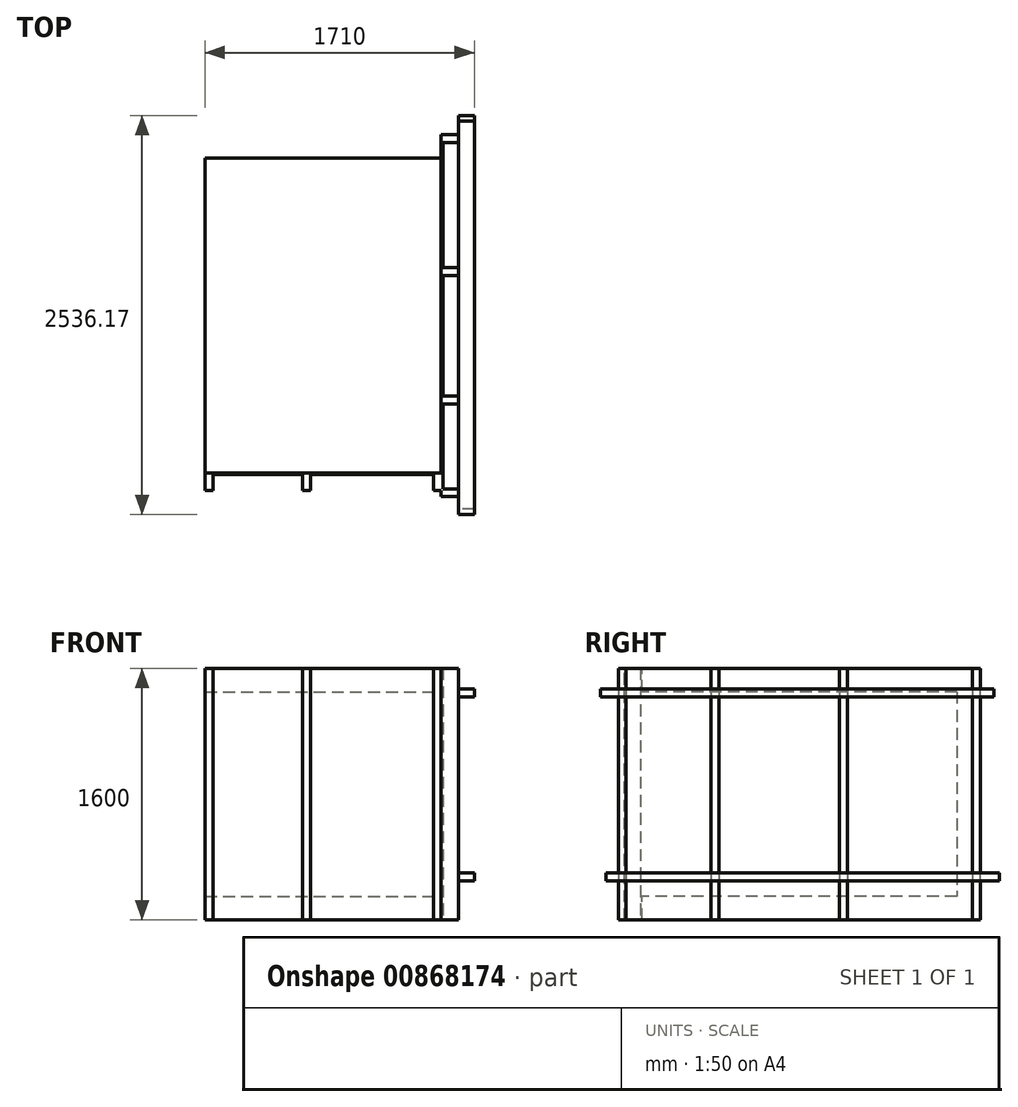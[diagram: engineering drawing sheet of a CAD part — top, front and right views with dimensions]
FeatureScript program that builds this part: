
annotation { "Feature Type Name" : "Feature", "Feature Type Description" : "" }
export const myFeature = defineFeature(function(context is Context, id is Id, definition is map)
    precondition{}
    {
        {
            var Q0;
            Q0=qCreatedBy(makeId("Top.planeOp"),FACE);
            var sketch = newSketch(context, id + "F0", { "sketchPlane" : qUnion([Q0])});
            skLineSegment(sketch, "E0.bottom", {"start": v(-1448.2, 1942.9) * mm, "end": v(51.8, 1942.9) * mm});
            skLineSegment(sketch, "E0.top", {"start": v(-1448.2, -57.1) * mm, "end": v(51.8, -57.1) * mm});
            skLineSegment(sketch, "E0.left", {"start": v(-1448.2, 1942.9) * mm, "end": v(-1448.2, -57.1) * mm});
            skLineSegment(sketch, "E0.right", {"start": v(51.8, 1942.9) * mm, "end": v(51.8, -57.1) * mm});
            skSolve(sketch);
        }
        {
            var Q0;
            Q0=makeQuery(id+"F0.imprint","IMPRINT",FACE,{"disambiguationData":[TD([[makeQuery(id+"F0.imprint","IMPRINT",EDGE,{"derivedFrom":sQuery(id+"F0.wireOp",EDGE,"E0.bottom")}),-1.0]])]});
            extrude(context, id + "F1", {"entities" : qUnion([Q0]), "depth" : 1300 * mm, "offsetDistance" : 25 * mm});
        }
        {
            var Q0;
            Q0=makeQuery(id+"F1.opExtrude","SWEPT_FACE",FACE,{"disambiguationData":[OSD([sQuery(id+"F0.wireOp",EDGE,"E0.right")])]});
            var sketch = newSketch(context, id + "F2", { "sketchPlane" : qUnion([Q0])});
            skLineSegment(sketch, "E1.bottom", {"start": v(-57.1, 1300) * mm, "end": v(1942.9, 1300) * mm});
            skLineSegment(sketch, "E1.top", {"start": v(-57.1, 0) * mm, "end": v(1942.9, 0) * mm});
            skLineSegment(sketch, "E1.left", {"start": v(-57.1, 1300) * mm, "end": v(-57.1, 0) * mm});
            skLineSegment(sketch, "E1.right", {"start": v(1942.9, 1300) * mm, "end": v(1942.9, 0) * mm});
            skLineSegment(sketch, "E2.0", {"start": v(-207.1, -150) * mm, "end": v(2092.9, -150) * mm});
            skLineSegment(sketch, "E2.1", {"start": v(-207.1, 1450) * mm, "end": v(-207.1, -150) * mm});
            skLineSegment(sketch, "E2.2", {"start": v(2092.9, 1450) * mm, "end": v(-207.1, 1450) * mm});
            skLineSegment(sketch, "E2.3", {"start": v(2092.9, -150) * mm, "end": v(2092.9, 1450) * mm});
            skSolve(sketch);
        }
        {
            var Q0;
            Q0=makeQuery(id+"F2.imprint","IMPRINT",FACE,{"disambiguationData":[TD([[makeQuery(id+"F2.imprint","IMPRINT",EDGE,{"derivedFrom":sQuery(id+"F2.wireOp",EDGE,"E1.bottom")}),-1.0]])]});
            var Q1;
            Q1=makeQuery(id+"F2.imprint","IMPRINT",FACE,{"disambiguationData":[TD([[makeQuery(id+"F2.imprint","IMPRINT",EDGE,{"derivedFrom":sQuery(id+"F2.wireOp",EDGE,"E1.bottom")}),1.0]])]});
            extrude(context, id + "F3", {"entities" : qUnion([Q0, Q1]), "operationType" : NewBodyOperationType.ADD, "depth" : 10 * mm, "offsetDistance" : 25 * mm});
        }
        {
            var Q0;
            Q0=makeQuery(id+"F3.opExtrude","CAP_FACE",FACE,{"disambiguationData":[OSD([sQuery(id+"F2.wireOp",EDGE,"E2.0"),sQuery(id+"F2.wireOp",EDGE,"E2.1"),sQuery(id+"F2.wireOp",EDGE,"E2.2"),sQuery(id+"F2.wireOp",EDGE,"E2.3")])],"isStart":false});
            var sketch = newSketch(context, id + "F4", { "sketchPlane" : qUnion([Q0])});
            skLineSegment(sketch, "E3.bottom", {"start": v(-207.1, 1450) * mm, "end": v(-157.1, 1450) * mm});
            skLineSegment(sketch, "E3.top", {"start": v(-207.1, -150) * mm, "end": v(-157.1, -150) * mm});
            skLineSegment(sketch, "E3.left", {"start": v(-207.1, 1450) * mm, "end": v(-207.1, -150) * mm});
            skLineSegment(sketch, "E3.right", {"start": v(-157.1, 1450) * mm, "end": v(-157.1, -150) * mm});
            skLineSegment(sketch, "E4.bottom", {"start": v(2042.9, 1450) * mm, "end": v(2092.9, 1450) * mm});
            skLineSegment(sketch, "E4.top", {"start": v(2042.9, -150) * mm, "end": v(2092.9, -150) * mm});
            skLineSegment(sketch, "E4.left", {"start": v(2042.9, 1450) * mm, "end": v(2042.9, -150) * mm});
            skLineSegment(sketch, "E4.right", {"start": v(2092.9, 1450) * mm, "end": v(2092.9, -150) * mm});
            skLineSegment(sketch, "E5.bottom", {"start": v(381.46, 1450) * mm, "end": v(431.46, 1450) * mm});
            skLineSegment(sketch, "E5.top", {"start": v(381.46, -150) * mm, "end": v(431.46, -150) * mm});
            skLineSegment(sketch, "E5.left", {"start": v(381.46, 1450) * mm, "end": v(381.46, -150) * mm});
            skLineSegment(sketch, "E5.right", {"start": v(431.46, 1450) * mm, "end": v(431.46, -150) * mm});
            skLineSegment(sketch, "E6.bottom", {"start": v(1197.73, 1450) * mm, "end": v(1247.73, 1450) * mm});
            skLineSegment(sketch, "E6.top", {"start": v(1197.73, -150) * mm, "end": v(1247.73, -150) * mm});
            skLineSegment(sketch, "E6.left", {"start": v(1197.73, 1450) * mm, "end": v(1197.73, -150) * mm});
            skLineSegment(sketch, "E6.right", {"start": v(1247.73, 1450) * mm, "end": v(1247.73, -150) * mm});
            skSolve(sketch);
        }
        {
            var Q0;
            Q0=makeQuery(id+"F4.imprint","IMPRINT",FACE,{"disambiguationData":[TD([[makeQuery(id+"F4.imprint","IMPRINT",EDGE,{"derivedFrom":sQuery(id+"F4.wireOp",EDGE,"E3.bottom")}),1.0]])]});
            var Q1;
            Q1=makeQuery(id+"F4.imprint","IMPRINT",FACE,{"disambiguationData":[TD([[makeQuery(id+"F4.imprint","IMPRINT",EDGE,{"derivedFrom":sQuery(id+"F4.wireOp",EDGE,"E5.bottom")}),1.0]])]});
            var Q2;
            Q2=makeQuery(id+"F4.imprint","IMPRINT",FACE,{"disambiguationData":[TD([[makeQuery(id+"F4.imprint","IMPRINT",EDGE,{"derivedFrom":sQuery(id+"F4.wireOp",EDGE,"E6.bottom")}),1.0]])]});
            var Q3;
            Q3=makeQuery(id+"F4.imprint","IMPRINT",FACE,{"disambiguationData":[TD([[makeQuery(id+"F4.imprint","IMPRINT",EDGE,{"derivedFrom":sQuery(id+"F4.wireOp",EDGE,"E4.bottom")}),1.0]])]});
            extrude(context, id + "F5", {"entities" : qUnion([Q0, Q1, Q2, Q3]), "operationType" : NewBodyOperationType.ADD, "depth" : 100 * mm, "offsetDistance" : 25 * mm});
        }
        {
            var Q0;
            Q0=makeQuery(id+"F5.opExtrude","CAP_FACE",FACE,{"disambiguationData":[OSD([sQuery(id+"F4.wireOp",EDGE,"E3.bottom"),sQuery(id+"F4.wireOp",EDGE,"E3.top"),sQuery(id+"F4.wireOp",EDGE,"E3.left"),sQuery(id+"F4.wireOp",EDGE,"E3.right")])],"isStart":false});
            var sketch = newSketch(context, id + "F6", { "sketchPlane" : qUnion([Q0])});
            skLineSegment(sketch, "E7.bottom", {"start": v(-321.49, 1317.57) * mm, "end": v(2178.51, 1317.57) * mm});
            skLineSegment(sketch, "E7.top", {"start": v(-321.49, 1267.57) * mm, "end": v(2178.51, 1267.57) * mm});
            skLineSegment(sketch, "E7.left", {"start": v(-321.49, 1317.57) * mm, "end": v(-321.49, 1267.57) * mm});
            skLineSegment(sketch, "E7.right", {"start": v(2178.51, 1317.57) * mm, "end": v(2178.51, 1267.57) * mm});
            skLineSegment(sketch, "E8.bottom", {"start": v(-285.32, 149.14) * mm, "end": v(2214.68, 149.14) * mm});
            skLineSegment(sketch, "E8.top", {"start": v(-285.32, 99.14) * mm, "end": v(2214.68, 99.14) * mm});
            skLineSegment(sketch, "E8.left", {"start": v(-285.32, 149.14) * mm, "end": v(-285.32, 99.14) * mm});
            skLineSegment(sketch, "E8.right", {"start": v(2214.68, 149.14) * mm, "end": v(2214.68, 99.14) * mm});
            skSolve(sketch);
        }
        {
            var Q0;
            {var subQ0=sQuery(id+"F6.wireOp",EDGE,"E7.left");Q0=makeQuery(id+"F6.imprint","IMPRINT",FACE,{"disambiguationData":[TD([[makeQuery(id+"F6.imprint","IMPRINT",EDGE,{"derivedFrom":subQ0}),1.0]])]});}
            var Q1;
            {var subQ0=sQuery(id+"F6.wireOp",EDGE,"E7.bottom");var subQ1=makeQuery(id+"F5.opExtrude","CAP_EDGE",EDGE,{"disambiguationData":[OSD([sQuery(id+"F4.wireOp",EDGE,"E3.left")])],"isStart":false});var subQ2=makeQuery(id+"F6.imprint","INTERSECT",VERTEX,{"derivedFrom":[subQ1,subQ0]});Q1=makeQuery(id+"F6.imprint","IMPRINT",FACE,{"disambiguationData":[TD([[makeQuery(id+"F6.imprint","IMPRINT",EDGE,{"disambiguationData":[TD([[subQ2,-1.0]])],"derivedFrom":subQ0}),-1.0]])]});}
            var Q2;
            {var subQ0=sQuery(id+"F6.wireOp",EDGE,"E7.right");Q2=makeQuery(id+"F6.imprint","IMPRINT",FACE,{"disambiguationData":[TD([[makeQuery(id+"F6.imprint","IMPRINT",EDGE,{"derivedFrom":subQ0}),-1.0]])]});}
            var Q3;
            {var subQ0=sQuery(id+"F6.wireOp",EDGE,"E8.right");Q3=makeQuery(id+"F6.imprint","IMPRINT",FACE,{"disambiguationData":[TD([[makeQuery(id+"F6.imprint","IMPRINT",EDGE,{"derivedFrom":subQ0}),-1.0]])]});}
            var Q4;
            {var subQ0=sQuery(id+"F6.wireOp",EDGE,"E8.bottom");var subQ1=makeQuery(id+"F5.opExtrude","CAP_EDGE",EDGE,{"disambiguationData":[OSD([sQuery(id+"F4.wireOp",EDGE,"E3.left")])],"isStart":false});var subQ2=makeQuery(id+"F6.imprint","INTERSECT",VERTEX,{"derivedFrom":[subQ1,subQ0]});Q4=makeQuery(id+"F6.imprint","IMPRINT",FACE,{"disambiguationData":[TD([[makeQuery(id+"F6.imprint","IMPRINT",EDGE,{"disambiguationData":[TD([[subQ2,-1.0]])],"derivedFrom":subQ0}),-1.0]])]});}
            var Q5;
            {var subQ0=sQuery(id+"F6.wireOp",EDGE,"E8.left");Q5=makeQuery(id+"F6.imprint","IMPRINT",FACE,{"disambiguationData":[TD([[makeQuery(id+"F6.imprint","IMPRINT",EDGE,{"derivedFrom":subQ0}),1.0]])]});}
            extrude(context, id + "F7", {"entities" : qUnion([Q0, Q1, Q2, Q3, Q4, Q5]), "operationType" : NewBodyOperationType.ADD, "depth" : 100 * mm, "offsetDistance" : 25 * mm});
        }
        {
            var Q0;
            Q0=makeQuery(id+"F1.opExtrude","SWEPT_FACE",FACE,{"disambiguationData":[OSD([sQuery(id+"F0.wireOp",EDGE,"E0.top")])]});
            var sketch = newSketch(context, id + "F8", { "sketchPlane" : qUnion([Q0])});
            skLineSegment(sketch, "E9.bottom", {"start": v(-1448.2, 1300) * mm, "end": v(51.8, 1300) * mm});
            skLineSegment(sketch, "E9.top", {"start": v(-1448.2, 1450) * mm, "end": v(51.8, 1450) * mm});
            skLineSegment(sketch, "E9.left", {"start": v(-1448.2, 1300) * mm, "end": v(-1448.2, 1450) * mm});
            skLineSegment(sketch, "E9.right", {"start": v(51.8, 1300) * mm, "end": v(51.8, 1450) * mm});
            skLineSegment(sketch, "E10.bottom", {"start": v(-1448.2, 0) * mm, "end": v(51.8, 0) * mm});
            skLineSegment(sketch, "E10.top", {"start": v(-1448.2, -150) * mm, "end": v(51.8, -150) * mm});
            skLineSegment(sketch, "E10.left", {"start": v(-1448.2, 0) * mm, "end": v(-1448.2, -150) * mm});
            skLineSegment(sketch, "E10.right", {"start": v(51.8, 0) * mm, "end": v(51.8, -150) * mm});
            skSolve(sketch);
        }
        {
            var Q0;
            Q0=makeQuery(id+"F8.imprint","IMPRINT",FACE,{"disambiguationData":[TD([[makeQuery(id+"F8.imprint","IMPRINT",EDGE,{"derivedFrom":sQuery(id+"F8.wireOp",EDGE,"E9.bottom")}),1.0]])]});
            var Q1;
            Q1=makeQuery(id+"F8.imprint","IMPRINT",FACE,{"disambiguationData":[TD([[makeQuery(id+"F8.imprint","IMPRINT",EDGE,{"derivedFrom":sQuery(id+"F8.wireOp",EDGE,"E9.bottom")}),-1.0]])]});
            var Q2;
            Q2=makeQuery(id+"F8.imprint","IMPRINT",FACE,{"disambiguationData":[TD([[makeQuery(id+"F8.imprint","IMPRINT",EDGE,{"derivedFrom":sQuery(id+"F8.wireOp",EDGE,"E10.bottom")}),-1.0]])]});
            extrude(context, id + "F9", {"entities" : qUnion([Q0, Q1, Q2]), "operationType" : NewBodyOperationType.ADD, "depth" : 10 * mm, "offsetDistance" : 25 * mm});
        }
        {
            var Q0;
            Q0=makeQuery(id+"F9.opExtrude","CAP_FACE",FACE,{"disambiguationData":[OSD([sQuery(id+"F0.wireOp",EDGE,"E0.top"),sQuery(id+"F0.wireOp",EDGE,"E0.left"),sQuery(id+"F0.wireOp",EDGE,"E0.right"),sQuery(id+"F8.wireOp",EDGE,"E9.top"),sQuery(id+"F8.wireOp",EDGE,"E9.left"),sQuery(id+"F8.wireOp",EDGE,"E9.right"),sQuery(id+"F8.wireOp",EDGE,"E10.top"),sQuery(id+"F8.wireOp",EDGE,"E10.left"),sQuery(id+"F8.wireOp",EDGE,"E10.right")])],"isStart":false});
            var sketch = newSketch(context, id + "F10", { "sketchPlane" : qUnion([Q0])});
            skLineSegment(sketch, "E11.bottom", {"start": v(-1448.2, 1450) * mm, "end": v(-1398.2, 1450) * mm});
            skLineSegment(sketch, "E11.top", {"start": v(-1448.2, -150) * mm, "end": v(-1398.2, -150) * mm});
            skLineSegment(sketch, "E11.left", {"start": v(-1448.2, 1450) * mm, "end": v(-1448.2, -150) * mm});
            skLineSegment(sketch, "E11.right", {"start": v(-1398.2, 1450) * mm, "end": v(-1398.2, -150) * mm});
            skLineSegment(sketch, "E12.bottom", {"start": v(1.8, 1450) * mm, "end": v(51.8, 1450) * mm});
            skLineSegment(sketch, "E12.top", {"start": v(1.8, -150) * mm, "end": v(51.8, -150) * mm});
            skLineSegment(sketch, "E12.left", {"start": v(1.8, 1450) * mm, "end": v(1.8, -150) * mm});
            skLineSegment(sketch, "E12.right", {"start": v(51.8, 1450) * mm, "end": v(51.8, -150) * mm});
            skLineSegment(sketch, "E13.bottom", {"start": v(-827.97, 1450) * mm, "end": v(-777.97, 1450) * mm});
            skLineSegment(sketch, "E13.top", {"start": v(-827.97, -150) * mm, "end": v(-777.97, -150) * mm});
            skLineSegment(sketch, "E13.left", {"start": v(-827.97, 1450) * mm, "end": v(-827.97, -150) * mm});
            skLineSegment(sketch, "E13.right", {"start": v(-777.97, 1450) * mm, "end": v(-777.97, -150) * mm});
            skSolve(sketch);
        }
        {
            var Q0;
            Q0=makeQuery(id+"F10.imprint","IMPRINT",FACE,{"disambiguationData":[TD([[makeQuery(id+"F10.imprint","IMPRINT",EDGE,{"derivedFrom":sQuery(id+"F10.wireOp",EDGE,"E12.bottom")}),-1.0]])]});
            var Q1;
            Q1=makeQuery(id+"F10.imprint","IMPRINT",FACE,{"disambiguationData":[TD([[makeQuery(id+"F10.imprint","IMPRINT",EDGE,{"derivedFrom":sQuery(id+"F10.wireOp",EDGE,"E13.bottom")}),-1.0]])]});
            var Q2;
            Q2=makeQuery(id+"F10.imprint","IMPRINT",FACE,{"disambiguationData":[TD([[makeQuery(id+"F10.imprint","IMPRINT",EDGE,{"derivedFrom":sQuery(id+"F10.wireOp",EDGE,"E11.bottom")}),-1.0]])]});
            extrude(context, id + "F11", {"entities" : qUnion([Q0, Q1, Q2]), "operationType" : NewBodyOperationType.ADD, "depth" : 100 * mm, "offsetDistance" : 25 * mm});
        }
    });
